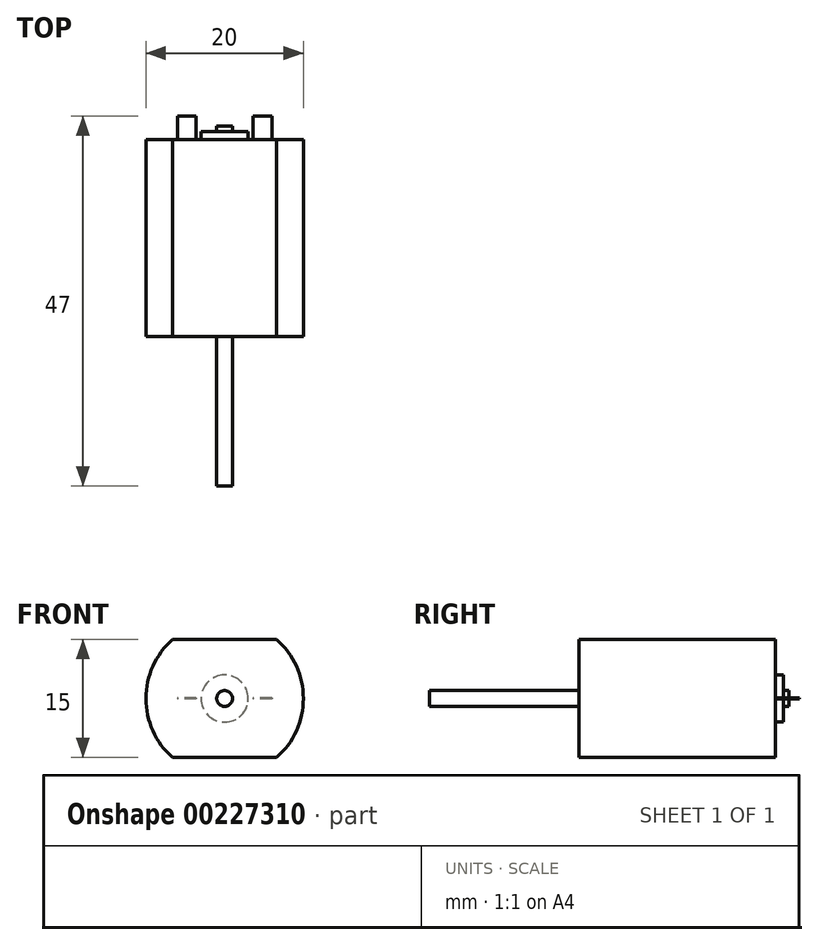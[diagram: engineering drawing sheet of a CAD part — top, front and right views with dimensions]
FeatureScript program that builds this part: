
annotation { "Feature Type Name" : "Feature", "Feature Type Description" : "" }
export const myFeature = defineFeature(function(context is Context, id is Id, definition is map)
    precondition{}
    {
        {
            var Q0;
            Q0=qCreatedBy(makeId("Front.planeOp"),FACE);
            var sketch = newSketch(context, id + "F0", { "sketchPlane" : qUnion([Q0])});
            skCircle(sketch, "E0", {"center": v(0, 0) * mm, "radius": 10 * mm, "construction": true});
            skLineSegment(sketch, "E1.bottom", {"start": v(-6.61, 7.5) * mm, "end": v(6.61, 7.5) * mm});
            skLineSegment(sketch, "E1.top", {"start": v(-6.61, -7.5) * mm, "end": v(6.61, -7.5) * mm});
            skLineSegment(sketch, "E1.left", {"start": v(-6.61, 7.5) * mm, "end": v(-6.61, -7.5) * mm, "construction": true});
            skLineSegment(sketch, "E1.right", {"start": v(6.61, 7.5) * mm, "end": v(6.61, -7.5) * mm, "construction": true});
            skArc(sketch, "E2", {"start": v(-6.61, -7.5) * mm, "mid": v(-10, 0) * mm, "end": v(-6.61, 7.5) * mm});
            skArc(sketch, "E3", {"start": v(6.61, 7.5) * mm, "mid": v(10, 0) * mm, "end": v(6.61, -7.5) * mm});
            skSolve(sketch);
        }
        {
            var Q0;
            Q0 = qSketchRegion(id + "F0", true);
            extrude(context, id + "F1", {"entities" : qUnion([Q0]), "depth" : 25 * mm});
        }
        {
            var Q0;
            Q0=makeQuery(id+"F1.opExtrude","CAP_FACE",FACE,{"disambiguationData":[OSD([sQuery(id+"F0.wireOp",EDGE,"E1.bottom"),sQuery(id+"F0.wireOp",EDGE,"E1.top"),sQuery(id+"F0.wireOp",EDGE,"E2"),sQuery(id+"F0.wireOp",EDGE,"E3")])],"isStart":true});
            var sketch = newSketch(context, id + "F2", { "sketchPlane" : qUnion([Q0])});
            skCircle(sketch, "E4", {"center": v(0, 0) * mm, "radius": 3 * mm});
            skCircle(sketch, "E5", {"center": v(0, 0) * mm, "radius": 1 * mm});
            skLineSegment(sketch, "E6.bottom", {"start": v(-6, 0.05) * mm, "end": v(-3.6, 0.05) * mm});
            skLineSegment(sketch, "E6.top", {"start": v(-6, -0.05) * mm, "end": v(-3.6, -0.05) * mm});
            skLineSegment(sketch, "E6.left", {"start": v(-6, 0.05) * mm, "end": v(-6, -0.05) * mm});
            skLineSegment(sketch, "E6.right", {"start": v(-3.6, 0.05) * mm, "end": v(-3.6, -0.05) * mm});
            skLineSegment(sketch, "E7.bottom", {"start": v(3.6, 0.05) * mm, "end": v(6, 0.05) * mm});
            skLineSegment(sketch, "E7.top", {"start": v(3.6, -0.05) * mm, "end": v(6, -0.05) * mm});
            skLineSegment(sketch, "E7.left", {"start": v(3.6, 0.05) * mm, "end": v(3.6, -0.05) * mm});
            skLineSegment(sketch, "E7.right", {"start": v(6, 0.05) * mm, "end": v(6, -0.05) * mm});
            skLineSegment(sketch, "E8", {"start": v(-10, 0) * mm, "end": v(10, 0) * mm, "construction": true});
            skPoint(sketch, "E9", {"position": v(-3.6, 0) * mm});
            skPoint(sketch, "E10", {"position": v(3.6, 0) * mm});
            skSolve(sketch);
        }
        {
            var Q0;
            Q0=makeQuery(id+"F2.imprint","IMPRINT",FACE,{"disambiguationData":[TD([[makeQuery(id+"F2.imprint","IMPRINT",EDGE,{"derivedFrom":sQuery(id+"F2.wireOp",EDGE,"E6.bottom")}),-1.0]])]});
            var Q1;
            Q1=makeQuery(id+"F2.imprint","IMPRINT",FACE,{"disambiguationData":[TD([[makeQuery(id+"F2.imprint","IMPRINT",EDGE,{"derivedFrom":sQuery(id+"F2.wireOp",EDGE,"E7.bottom")}),-1.0]])]});
            extrude(context, id + "F3", {"entities" : qUnion([Q0, Q1]), "operationType" : NewBodyOperationType.ADD, "depth" : 3 * mm});
        }
        {
            var Q0;
            Q0=makeQuery(id+"F1.opExtrude","CAP_FACE",FACE,{"disambiguationData":[OSD([sQuery(id+"F0.wireOp",EDGE,"E1.bottom"),sQuery(id+"F0.wireOp",EDGE,"E1.top"),sQuery(id+"F0.wireOp",EDGE,"E2"),sQuery(id+"F0.wireOp",EDGE,"E3")])],"isStart":true});
            var sketch = newSketch(context, id + "F4", { "sketchPlane" : qUnion([Q0])});
            skCircle(sketch, "E11", {"center": v(0, 0) * mm, "radius": 3 * mm});
            skCircle(sketch, "E12", {"center": v(0, 0) * mm, "radius": 1 * mm});
            skLineSegment(sketch, "E13.bottom", {"start": v(-6, 0.05) * mm, "end": v(-3.6, 0.05) * mm});
            skLineSegment(sketch, "E13.top", {"start": v(-6, -0.05) * mm, "end": v(-3.6, -0.05) * mm});
            skLineSegment(sketch, "E13.left", {"start": v(-6, 0.05) * mm, "end": v(-6, -0.05) * mm});
            skLineSegment(sketch, "E13.right", {"start": v(-3.6, 0.05) * mm, "end": v(-3.6, -0.05) * mm});
            skLineSegment(sketch, "E14.bottom", {"start": v(3.6, 0.05) * mm, "end": v(6, 0.05) * mm});
            skLineSegment(sketch, "E14.top", {"start": v(3.6, -0.05) * mm, "end": v(6, -0.05) * mm});
            skLineSegment(sketch, "E14.left", {"start": v(3.6, 0.05) * mm, "end": v(3.6, -0.05) * mm});
            skLineSegment(sketch, "E14.right", {"start": v(6, 0.05) * mm, "end": v(6, -0.05) * mm});
            skLineSegment(sketch, "E15", {"start": v(-10, 0) * mm, "end": v(10, 0) * mm, "construction": true});
            skPoint(sketch, "E16", {"position": v(-3.6, 0) * mm});
            skPoint(sketch, "E17", {"position": v(3.6, 0) * mm});
            skSolve(sketch);
        }
        {
            var Q0;
            Q0=makeQuery(id+"F4.imprint","IMPRINT",FACE,{"disambiguationData":[TD([[makeQuery(id+"F4.imprint","IMPRINT",EDGE,{"derivedFrom":sQuery(id+"F4.wireOp",EDGE,"E11")}),1.0]])]});
            extrude(context, id + "F5", {"entities" : qUnion([Q0]), "operationType" : NewBodyOperationType.ADD, "depth" : 1 * mm});
        }
        {
            var Q0;
            {var subQ0=sQuery(id+"F0.wireOp",EDGE,"E2");var subQ1=sQuery(id+"F0.wireOp",EDGE,"E1.bottom");var subQ2=sQuery(id+"F0.wireOp",EDGE,"E1.top");var subQ3=sQuery(id+"F0.wireOp",EDGE,"E3");Q0=makeQuery(id+"F5.boolean.opBoolean","SPLIT",FACE,{"disambiguationData":[TD([makeQuery(id+"F1.opExtrude","SWEPT_FACE",FACE,{"disambiguationData":[OSD([subQ1])]})])],"derivedFrom":makeQuery(id+"F1.opExtrude","CAP_FACE",FACE,{"disambiguationData":[OSD([subQ1,subQ2,subQ0,subQ3])],"isStart":true})});}
            var sketch = newSketch(context, id + "F6", { "sketchPlane" : qUnion([Q0])});
            skCircle(sketch, "E18", {"center": v(0, 0) * mm, "radius": 3 * mm});
            skCircle(sketch, "E19", {"center": v(0, 0) * mm, "radius": 1 * mm});
            skLineSegment(sketch, "E20.bottom", {"start": v(-6, 0.05) * mm, "end": v(-3.6, 0.05) * mm});
            skLineSegment(sketch, "E20.top", {"start": v(-6, -0.05) * mm, "end": v(-3.6, -0.05) * mm});
            skLineSegment(sketch, "E20.left", {"start": v(-6, 0.05) * mm, "end": v(-6, -0.05) * mm});
            skLineSegment(sketch, "E20.right", {"start": v(-3.6, 0.05) * mm, "end": v(-3.6, -0.05) * mm});
            skLineSegment(sketch, "E21.bottom", {"start": v(3.6, 0.05) * mm, "end": v(6, 0.05) * mm});
            skLineSegment(sketch, "E21.top", {"start": v(3.6, -0.05) * mm, "end": v(6, -0.05) * mm});
            skLineSegment(sketch, "E21.left", {"start": v(3.6, 0.05) * mm, "end": v(3.6, -0.05) * mm});
            skLineSegment(sketch, "E21.right", {"start": v(6, 0.05) * mm, "end": v(6, -0.05) * mm});
            skLineSegment(sketch, "E22", {"start": v(-10, 0) * mm, "end": v(10, 0) * mm, "construction": true});
            skPoint(sketch, "E23", {"position": v(-3.6, 0) * mm});
            skPoint(sketch, "E24", {"position": v(3.6, 0) * mm});
            skSolve(sketch);
        }
        {
            var Q0;
            Q0=makeQuery(id+"F6.imprint","IMPRINT",FACE,{"disambiguationData":[TD([[makeQuery(id+"F6.imprint","IMPRINT",EDGE,{"derivedFrom":sQuery(id+"F6.wireOp",EDGE,"E19")}),1.0]])]});
            extrude(context, id + "F7", {"entities" : qUnion([Q0]), "operationType" : NewBodyOperationType.ADD, "depth" : 1.7 * mm});
        }
        {
            var Q0;
            Q0=makeQuery(id+"F1.opExtrude","CAP_FACE",FACE,{"disambiguationData":[OSD([sQuery(id+"F0.wireOp",EDGE,"E1.bottom"),sQuery(id+"F0.wireOp",EDGE,"E1.top"),sQuery(id+"F0.wireOp",EDGE,"E2"),sQuery(id+"F0.wireOp",EDGE,"E3")])],"isStart":false});
            var sketch = newSketch(context, id + "F8", { "sketchPlane" : qUnion([Q0])});
            skCircle(sketch, "E25", {"center": v(0, 0) * mm, "radius": 1 * mm});
            skSolve(sketch);
        }
        {
            var Q0;
            Q0 = qSketchRegion(id + "F8", true);
            extrude(context, id + "F9", {"entities" : qUnion([Q0]), "operationType" : NewBodyOperationType.ADD, "depth" : 19 * mm});
        }
    });
